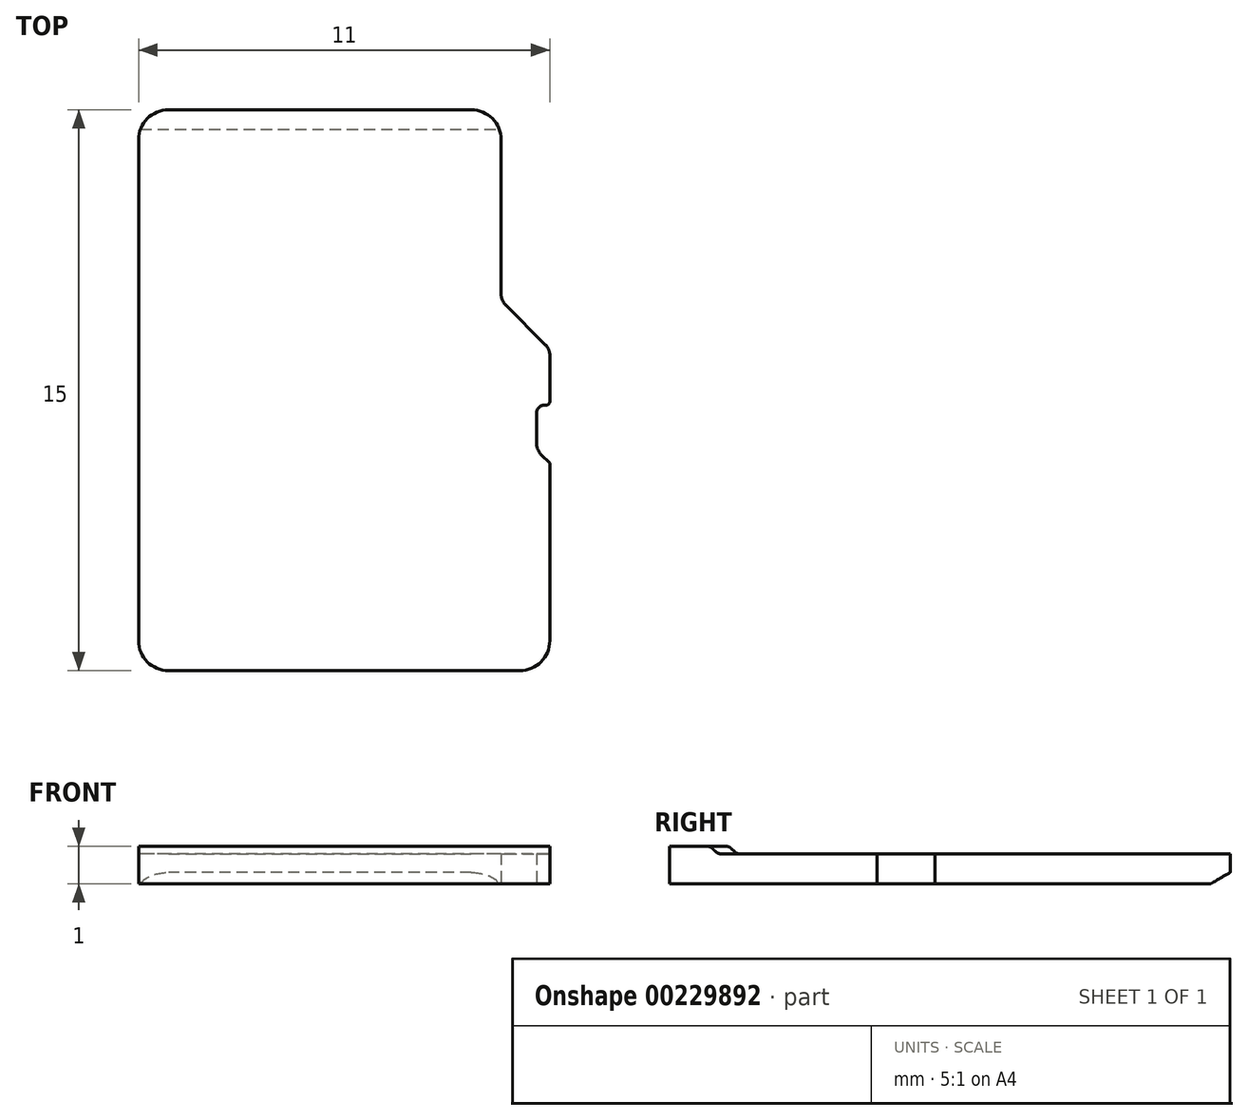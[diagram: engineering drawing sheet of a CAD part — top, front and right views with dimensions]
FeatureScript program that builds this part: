
annotation { "Feature Type Name" : "Feature", "Feature Type Description" : "" }
export const myFeature = defineFeature(function(context is Context, id is Id, definition is map)
    precondition{}
    {
        {
            var Q0;
            Q0=qCreatedBy(makeId("Top.planeOp"),FACE);
            var sketch = newSketch(context, id + "F0", { "sketchPlane" : qUnion([Q0])});
            skLineSegment(sketch, "E0.bottom", {"start": v(-0.8, 0) * mm, "end": v(-10.2, 0) * mm});
            skLineSegment(sketch, "E0.top", {"start": v(0, 15) * mm, "end": v(-11, 15) * mm, "construction": true});
            skLineSegment(sketch, "E0.left", {"start": v(0, 0) * mm, "end": v(0, 5.55) * mm, "construction": true});
            skLineSegment(sketch, "E0.right", {"start": v(-11, 0.8) * mm, "end": v(-11, 14.2) * mm});
            skLineSegment(sketch, "E1", {"start": v(-1.3, 14.2) * mm, "end": v(-1.3, 10.07) * mm});
            skLineSegment(sketch, "E2", {"start": v(-1.18, 9.78) * mm, "end": v(-0.12, 8.72) * mm});
            skLineSegment(sketch, "E3", {"start": v(-10.2, 15) * mm, "end": v(-2.1, 15) * mm});
            skLineSegment(sketch, "E4", {"start": v(0, 8.43) * mm, "end": v(0, 7.2) * mm});
            skPoint(sketch, "E5.visualSharp", {"position": v(-1.3, 15) * mm});
            skArc(sketch, "E5.filletArc", {"start": v(-1.3, 14.2) * mm, "mid": v(-1.53, 14.77) * mm, "end": v(-2.1, 15) * mm});
            skPoint(sketch, "E6.visualSharp", {"position": v(-11, 15) * mm});
            skArc(sketch, "E6.filletArc", {"start": v(-10.2, 15) * mm, "mid": v(-10.77, 14.77) * mm, "end": v(-11, 14.2) * mm});
            skPoint(sketch, "E7.visualSharp", {"position": v(-11, 0) * mm});
            skArc(sketch, "E7.filletArc", {"start": v(-11, 0.8) * mm, "mid": v(-10.77, 0.23) * mm, "end": v(-10.2, 0) * mm});
            skPoint(sketch, "E8.visualSharp", {"position": v(0, 0) * mm});
            skArc(sketch, "E8.filletArc", {"start": v(-0.8, 0) * mm, "mid": v(-0.23, 0.23) * mm, "end": v(0, 0.8) * mm});
            skPoint(sketch, "E9.visualSharp", {"position": v(-1.3, 9.9) * mm});
            skArc(sketch, "E9.filletArc", {"start": v(-1.3, 10.07) * mm, "mid": v(-1.27, 9.91) * mm, "end": v(-1.18, 9.78) * mm});
            skArc(sketch, "E10", {"start": v(0, 1.33) * mm, "mid": v(-5.5, 1.84) * mm, "end": v(-11, 1.33) * mm});
            skArc(sketch, "E11", {"start": v(0, 1) * mm, "mid": v(-5.5, 1.5) * mm, "end": v(-11, 1) * mm});
            skLineSegment(sketch, "E12", {"start": v(-0.1, 7.1) * mm, "end": v(-0.15, 7.1) * mm});
            skLineSegment(sketch, "E13", {"start": v(-0.35, 6.9) * mm, "end": v(-0.35, 6.07) * mm});
            skLineSegment(sketch, "E14", {"start": v(-0.23, 5.78) * mm, "end": v(0, 5.55) * mm});
            skLineSegment(sketch, "E15.trimOffspring", {"start": v(0, 7.1) * mm, "end": v(0, 15) * mm, "construction": true});
            skLineSegment(sketch, "E16.trimOffspring", {"start": v(0, 5.55) * mm, "end": v(0, 0.8) * mm});
            skPoint(sketch, "E17.visualSharp", {"position": v(-0.35, 5.9) * mm});
            skArc(sketch, "E17.filletArc", {"start": v(-0.35, 6.07) * mm, "mid": v(-0.32, 5.91) * mm, "end": v(-0.23, 5.78) * mm});
            skPoint(sketch, "E18.visualSharp", {"position": v(-0.35, 7.1) * mm});
            skArc(sketch, "E18.filletArc", {"start": v(-0.15, 7.1) * mm, "mid": v(-0.3, 7.04) * mm, "end": v(-0.35, 6.9) * mm});
            skPoint(sketch, "E19.visualSharp", {"position": v(0, 7.1) * mm});
            skArc(sketch, "E19.filletArc", {"start": v(-0.1, 7.1) * mm, "mid": v(-0.03, 7.13) * mm, "end": v(0, 7.2) * mm});
            skPoint(sketch, "E20.visualSharp", {"position": v(0, 8.6) * mm});
            skArc(sketch, "E20.filletArc", {"start": v(0, 8.43) * mm, "mid": v(-0.03, 8.59) * mm, "end": v(-0.12, 8.72) * mm});
            skSolve(sketch);
        }
        {
            var Q0;
            Q0 = qSketchRegion(id + "F0", true);
            extrude(context, id + "F1", {"entities" : qUnion([Q0]), "depth" : .8 * mm});
        }
        {
            var Q0;
            Q0=makeQuery(id+"F0.imprint","IMPRINT",FACE,{"disambiguationData":[TD([[makeQuery(id+"F0.imprint","IMPRINT",EDGE,{"derivedFrom":sQuery(id+"F0.wireOp",EDGE,"E0.bottom")}),-1.0]])]});
            extrude(context, id + "F2", {"entities" : qUnion([Q0]), "operationType" : NewBodyOperationType.ADD, "depth" : 1 * mm});
        }
        {
            var Q0;
            Q0=makeQuery(id+"F2.boolean.opBoolean","INTERSECT",EDGE,{"derivedFrom":[makeQuery(id+"F1.opExtrude","CAP_FACE",FACE,{"disambiguationData":[OSD([sQuery(id+"F0.wireOp",EDGE,"E0.bottom"),sQuery(id+"F0.wireOp",EDGE,"E0.right"),sQuery(id+"F0.wireOp",EDGE,"E1"),sQuery(id+"F0.wireOp",EDGE,"E2"),sQuery(id+"F0.wireOp",EDGE,"E3"),sQuery(id+"F0.wireOp",EDGE,"E4"),sQuery(id+"F0.wireOp",EDGE,"E5.filletArc"),sQuery(id+"F0.wireOp",EDGE,"E6.filletArc"),sQuery(id+"F0.wireOp",EDGE,"E7.filletArc"),sQuery(id+"F0.wireOp",EDGE,"E8.filletArc"),sQuery(id+"F0.wireOp",EDGE,"E9.filletArc"),sQuery(id+"F0.wireOp",EDGE,"E12"),sQuery(id+"F0.wireOp",EDGE,"E13"),sQuery(id+"F0.wireOp",EDGE,"E14"),sQuery(id+"F0.wireOp",EDGE,"E16.trimOffspring"),sQuery(id+"F0.wireOp",EDGE,"E17.filletArc"),sQuery(id+"F0.wireOp",EDGE,"E18.filletArc"),sQuery(id+"F0.wireOp",EDGE,"E19.filletArc"),sQuery(id+"F0.wireOp",EDGE,"E20.filletArc")])],"isStart":false}),makeQuery(id+"F2.opExtrude","SWEPT_FACE",FACE,{"disambiguationData":[OSD([sQuery(id+"F0.wireOp",EDGE,"E11")])]})]});
            chamfer(context, id + "F3", {"entities" : qUnion([Q0]), "width" : .3 * mm, "tangentPropagation" : true});
        }
        {
            var Q0;
            {var subQ0=makeQuery(id+"F1.opExtrude","CAP_FACE",FACE,{"disambiguationData":[OSD([sQuery(id+"F0.wireOp",EDGE,"E0.bottom"),sQuery(id+"F0.wireOp",EDGE,"E0.right"),sQuery(id+"F0.wireOp",EDGE,"E1"),sQuery(id+"F0.wireOp",EDGE,"E2"),sQuery(id+"F0.wireOp",EDGE,"E3"),sQuery(id+"F0.wireOp",EDGE,"E4"),sQuery(id+"F0.wireOp",EDGE,"E5.filletArc"),sQuery(id+"F0.wireOp",EDGE,"E6.filletArc"),sQuery(id+"F0.wireOp",EDGE,"E7.filletArc"),sQuery(id+"F0.wireOp",EDGE,"E8.filletArc"),sQuery(id+"F0.wireOp",EDGE,"E9.filletArc"),sQuery(id+"F0.wireOp",EDGE,"E12"),sQuery(id+"F0.wireOp",EDGE,"E13"),sQuery(id+"F0.wireOp",EDGE,"E14"),sQuery(id+"F0.wireOp",EDGE,"E16.trimOffspring"),sQuery(id+"F0.wireOp",EDGE,"E17.filletArc"),sQuery(id+"F0.wireOp",EDGE,"E18.filletArc"),sQuery(id+"F0.wireOp",EDGE,"E19.filletArc"),sQuery(id+"F0.wireOp",EDGE,"E20.filletArc")])],"isStart":false});Q0=makeQuery(id+"F3.opChamfer","BLEND_EDGE",EDGE,{"blendedFrom":[makeQuery(id+"F2.boolean.opBoolean","INTERSECT",EDGE,{"derivedFrom":[subQ0,makeQuery(id+"F2.opExtrude","SWEPT_FACE",FACE,{"disambiguationData":[OSD([sQuery(id+"F0.wireOp",EDGE,"E11")])]})]}),subQ0],"blendedInto":[subQ0]});}
            var Q1;
            {var subQ0=sQuery(id+"F0.wireOp",EDGE,"E16.trimOffspring");var subQ1=sQuery(id+"F0.wireOp",EDGE,"E11");var subQ2=sQuery(id+"F0.wireOp",EDGE,"E8.filletArc");var subQ3=sQuery(id+"F0.wireOp",EDGE,"E7.filletArc");var subQ4=sQuery(id+"F0.wireOp",EDGE,"E0.right");var subQ5=sQuery(id+"F0.wireOp",EDGE,"E0.bottom");Q1=makeQuery(id+"F3.opChamfer","BLEND_EDGE",EDGE,{"blendedFrom":[makeQuery(id+"F2.boolean.opBoolean","INTERSECT",EDGE,{"derivedFrom":[makeQuery(id+"F1.opExtrude","CAP_FACE",FACE,{"disambiguationData":[OSD([subQ5,subQ4,sQuery(id+"F0.wireOp",EDGE,"E1"),sQuery(id+"F0.wireOp",EDGE,"E2"),sQuery(id+"F0.wireOp",EDGE,"E3"),sQuery(id+"F0.wireOp",EDGE,"E4"),sQuery(id+"F0.wireOp",EDGE,"E5.filletArc"),sQuery(id+"F0.wireOp",EDGE,"E6.filletArc"),subQ3,subQ2,sQuery(id+"F0.wireOp",EDGE,"E9.filletArc"),sQuery(id+"F0.wireOp",EDGE,"E12"),sQuery(id+"F0.wireOp",EDGE,"E13"),sQuery(id+"F0.wireOp",EDGE,"E14"),subQ0,sQuery(id+"F0.wireOp",EDGE,"E17.filletArc"),sQuery(id+"F0.wireOp",EDGE,"E18.filletArc"),sQuery(id+"F0.wireOp",EDGE,"E19.filletArc"),sQuery(id+"F0.wireOp",EDGE,"E20.filletArc")])],"isStart":false}),makeQuery(id+"F2.opExtrude","SWEPT_FACE",FACE,{"disambiguationData":[OSD([subQ1])]})]}),makeQuery(id+"F2.opExtrude","CAP_FACE",FACE,{"disambiguationData":[OSD([subQ5,subQ4,subQ3,subQ2,subQ1,subQ0])],"isStart":false})],"blendedInto":[makeQuery(id+"F2.opExtrude","CAP_FACE",FACE,{"disambiguationData":[OSD([subQ5,subQ4,subQ3,subQ2,subQ1,subQ0])],"isStart":false})]});}
            fillet(context, id + "F4", {"entities" : qUnion([Q0, Q1]), "radius" : .2 * mm, "tangentPropagation" : true, "allowEdgeOverflow" : false});
        }
        {
            var Q0;
            Q0=makeQuery(id+"F1.opExtrude","CAP_EDGE",EDGE,{"disambiguationData":[OSD([sQuery(id+"F0.wireOp",EDGE,"E3")])],"isStart":true});
            chamfer(context, id + "F5", {"entities" : qUnion([Q0]), "chamferType" : ChamferType.TWO_OFFSETS, "width1" : .52 * mm, "oppositeDirection" : false, "width2" : .3 * mm});
        }
    });
